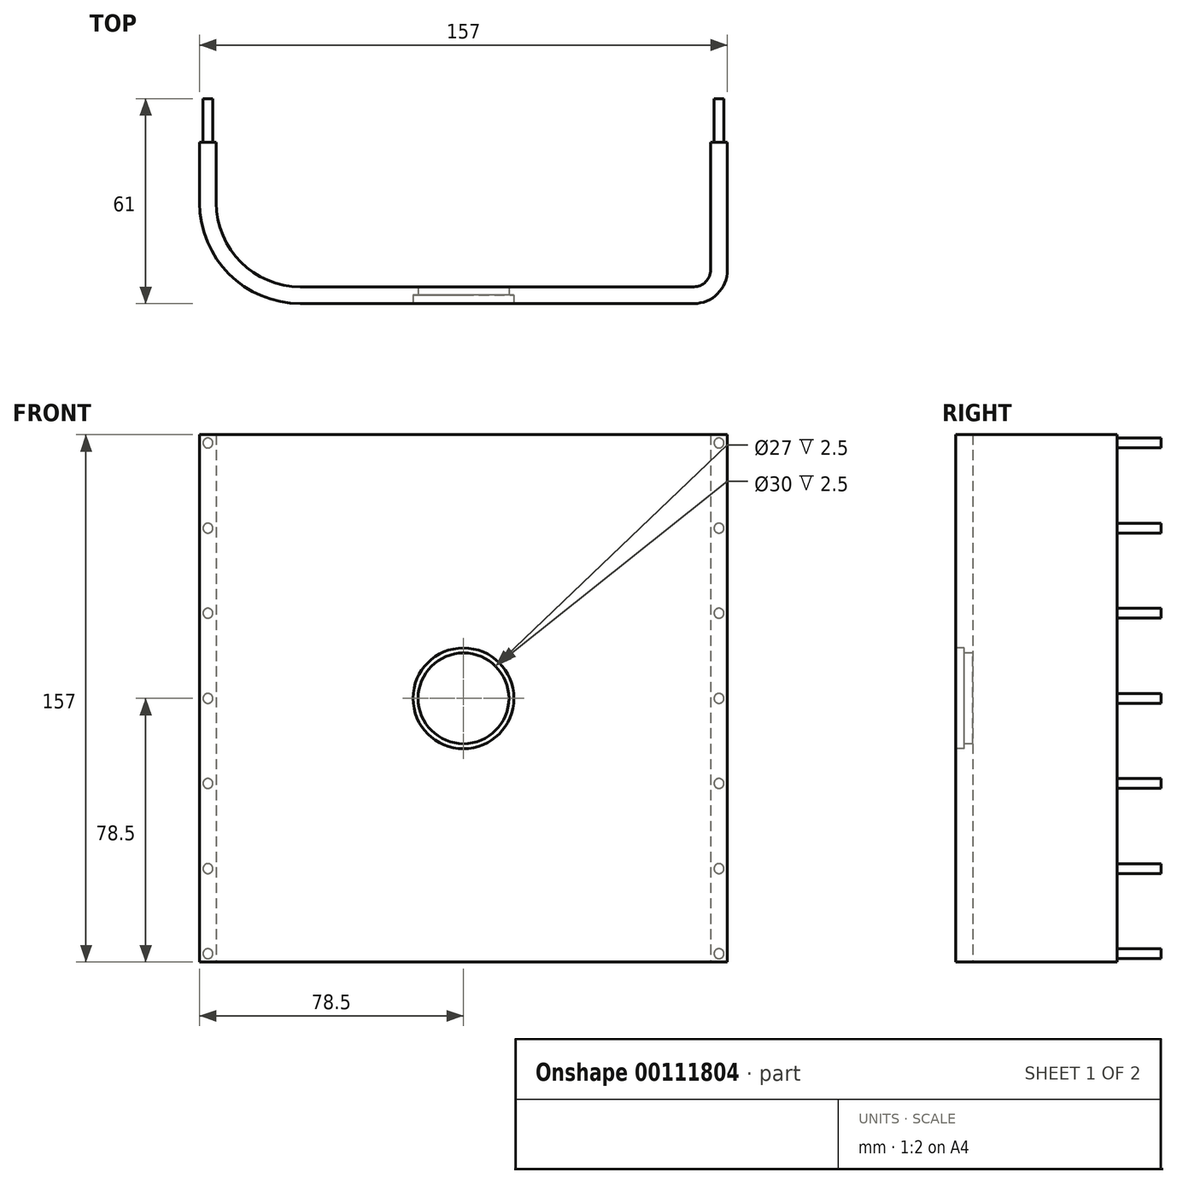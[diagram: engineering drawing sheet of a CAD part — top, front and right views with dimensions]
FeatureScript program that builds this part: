
annotation { "Feature Type Name" : "Feature", "Feature Type Description" : "" }
export const myFeature = defineFeature(function(context is Context, id is Id, definition is map)
    precondition{}
    {
        {
            var Q0;
            Q0=qCreatedBy(makeId("Top.planeOp"),FACE);
            var sketch = newSketch(context, id + "F0", { "sketchPlane" : qUnion([Q0])});
            skLineSegment(sketch, "E0.bottom", {"start": v(68.5, -24) * mm, "end": v(-48.5, -24) * mm});
            skLineSegment(sketch, "E0.top", {"start": v(78.5, 24) * mm, "end": v(-78.5, 24) * mm});
            skLineSegment(sketch, "E0.left", {"start": v(78.5, -14) * mm, "end": v(78.5, 24) * mm});
            skLineSegment(sketch, "E0.right", {"start": v(-78.5, 6) * mm, "end": v(-78.5, 24) * mm});
            skPoint(sketch, "E0.middle", {"position": v(0, 0) * mm});
            skPoint(sketch, "E1.visualSharp", {"position": v(78.5, -24) * mm});
            skArc(sketch, "E1.filletArc", {"start": v(68.5, -24) * mm, "mid": v(75.57, -21.07) * mm, "end": v(78.5, -14) * mm});
            skPoint(sketch, "E2.visualSharp", {"position": v(-78.5, -24) * mm});
            skArc(sketch, "E2.filletArc", {"start": v(-78.5, 6) * mm, "mid": v(-69.71, -15.21) * mm, "end": v(-48.5, -24) * mm});
            skLineSegment(sketch, "E3.bottom", {"start": v(68.5, -19) * mm, "end": v(-48.5, -19) * mm});
            skLineSegment(sketch, "E3.left", {"start": v(73.5, -14) * mm, "end": v(73.5, 24) * mm});
            skLineSegment(sketch, "E3.right", {"start": v(-73.5, 6) * mm, "end": v(-73.5, 24) * mm});
            skPoint(sketch, "E4.visualSharp", {"position": v(-73.5, -19) * mm});
            skArc(sketch, "E4.filletArc", {"start": v(-73.5, 6) * mm, "mid": v(-66.18, -11.68) * mm, "end": v(-48.5, -19) * mm});
            skPoint(sketch, "E5.visualSharp", {"position": v(73.5, -19) * mm});
            skArc(sketch, "E5.filletArc", {"start": v(68.5, -19) * mm, "mid": v(72.04, -17.54) * mm, "end": v(73.5, -14) * mm});
            skSolve(sketch);
        }
        {
            var Q0;
            Q0=makeQuery(id+"F0.imprint","IMPRINT",FACE,{"disambiguationData":[TD([[makeQuery(id+"F0.imprint","IMPRINT",EDGE,{"derivedFrom":sQuery(id+"F0.wireOp",EDGE,"E0.bottom")}),-1.0]])]});
            extrude(context, id + "F1", {"entities" : qUnion([Q0]), "depth" : 157 * mm});
        }
        {
            var Q0;
            Q0=makeQuery(id+"F1.opExtrude","SWEPT_FACE",FACE,{"disambiguationData":[OSD([sQuery(id+"F0.wireOp",EDGE,"E0.bottom")])]});
            var sketch = newSketch(context, id + "F2", { "sketchPlane" : qUnion([Q0])});
            skCircle(sketch, "E6", {"center": v(0, 78.5) * mm, "radius": 13.5 * mm});
            skSolve(sketch);
        }
        {
            var Q0;
            Q0=makeQuery(id+"F2.imprint","IMPRINT",FACE,{"disambiguationData":[TD([[makeQuery(id+"F2.imprint","IMPRINT",EDGE,{"derivedFrom":sQuery(id+"F2.wireOp",EDGE,"E6")}),1.0]])]});
            extrude(context, id + "F3", {"entities" : qUnion([Q0]), "operationType" : NewBodyOperationType.REMOVE, "oppositeDirection" : true, "depth" : 25 * mm});
        }
        {
            var Q0;
            Q0=makeQuery(id+"F1.opExtrude","SWEPT_FACE",FACE,{"disambiguationData":[OSD([sQuery(id+"F0.wireOp",EDGE,"E0.bottom")])]});
            var sketch = newSketch(context, id + "F4", { "sketchPlane" : qUnion([Q0])});
            skCircle(sketch, "E7", {"center": v(0, 78.5) * mm, "radius": 15 * mm});
            skSolve(sketch);
        }
        {
            var Q0;
            Q0 = qSketchRegion(id + "F4", true);
            extrude(context, id + "F5", {"entities" : qUnion([Q0]), "operationType" : NewBodyOperationType.REMOVE, "oppositeDirection" : true, "depth" : 2.5 * mm});
        }
        {
            var Q0;
            {var subQ0=sQuery(id+"F0.wireOp",EDGE,"E0.top");Q0=makeQuery(id+"F1.opExtrude","SWEPT_FACE",FACE,{"disambiguationData":[OSD([subQ0]),TDD([makeQuery(id+"F0.imprint","IMPRINT",EDGE,{"disambiguationData":[TD([[makeQuery(id+"F0.imprint","INTERSECT",VERTEX,{"derivedFrom":[subQ0,sQuery(id+"F0.wireOp",EDGE,"E0.right")]}),1.0]])],"derivedFrom":subQ0})])]});}
            var sketch = newSketch(context, id + "F6", { "sketchPlane" : qUnion([Q0])});
            skCircle(sketch, "E8", {"center": v(-76, 154.5) * mm, "radius": 1.48 * mm});
            skCircle(sketch, "E9.0.1.0", {"center": v(-76, 129.17) * mm, "radius": 1.48 * mm});
            skCircle(sketch, "E9.0.2.0", {"center": v(-76, 103.83) * mm, "radius": 1.48 * mm});
            skCircle(sketch, "E9.0.3.0", {"center": v(-76, 78.5) * mm, "radius": 1.48 * mm});
            skCircle(sketch, "E9.0.4.0", {"center": v(-76, 53.17) * mm, "radius": 1.48 * mm});
            skCircle(sketch, "E9.0.5.0", {"center": v(-76, 27.83) * mm, "radius": 1.48 * mm});
            skCircle(sketch, "E9.0.6.0", {"center": v(-76, 2.5) * mm, "radius": 1.48 * mm});
            skLineSegment(sketch, "E9.direction1", {"start": v(-76, 154.5) * mm, "end": v(-51, 154.5) * mm, "construction": true});
            skLineSegment(sketch, "E9.direction2", {"start": v(-76, 154.5) * mm, "end": v(-76, 129.17) * mm, "construction": true});
            skSolve(sketch);
        }
        {
            var Q0;
            Q0 = qSketchRegion(id + "F6", true);
            extrude(context, id + "F7", {"entities" : qUnion([Q0]), "operationType" : NewBodyOperationType.ADD, "depth" : 13 * mm});
        }
        {
            var Q0;
            {var subQ0=sQuery(id+"F0.wireOp",EDGE,"E0.top");Q0=makeQuery(id+"F1.opExtrude","SWEPT_FACE",FACE,{"disambiguationData":[OSD([subQ0]),TDD([makeQuery(id+"F0.imprint","IMPRINT",EDGE,{"disambiguationData":[TD([[makeQuery(id+"F0.imprint","INTERSECT",VERTEX,{"derivedFrom":[subQ0,sQuery(id+"F0.wireOp",EDGE,"E0.right")]}),1.0]])],"derivedFrom":subQ0})])]});}
            var sketch = newSketch(context, id + "F8", { "sketchPlane" : qUnion([Q0])});
            skCircle(sketch, "E10", {"center": v(76, 154.5) * mm, "radius": 1.48 * mm});
            skCircle(sketch, "E11.0.1.0", {"center": v(76, 129.17) * mm, "radius": 1.48 * mm});
            skCircle(sketch, "E11.0.2.0", {"center": v(76, 103.83) * mm, "radius": 1.48 * mm});
            skCircle(sketch, "E11.0.3.0", {"center": v(76, 78.5) * mm, "radius": 1.48 * mm});
            skCircle(sketch, "E11.0.4.0", {"center": v(76, 53.17) * mm, "radius": 1.48 * mm});
            skCircle(sketch, "E11.0.5.0", {"center": v(76, 27.83) * mm, "radius": 1.48 * mm});
            skCircle(sketch, "E11.0.6.0", {"center": v(76, 2.5) * mm, "radius": 1.48 * mm});
            skLineSegment(sketch, "E11.direction1", {"start": v(76, 154.5) * mm, "end": v(101, 154.5) * mm, "construction": true});
            skLineSegment(sketch, "E11.direction2", {"start": v(76, 154.5) * mm, "end": v(76, 129.17) * mm, "construction": true});
            skSolve(sketch);
        }
        {
            var Q0;
            Q0=makeQuery(id+"F8.imprint","IMPRINT",FACE,{"disambiguationData":[TD([[makeQuery(id+"F8.imprint","IMPRINT",EDGE,{"derivedFrom":sQuery(id+"F8.wireOp",EDGE,"E11.0.2.0")}),1.0]])]});
            var Q1;
            Q1=makeQuery(id+"F8.imprint","IMPRINT",FACE,{"disambiguationData":[TD([[makeQuery(id+"F8.imprint","IMPRINT",EDGE,{"derivedFrom":sQuery(id+"F8.wireOp",EDGE,"E11.0.1.0")}),1.0]])]});
            var Q2;
            Q2=makeQuery(id+"F8.imprint","IMPRINT",FACE,{"disambiguationData":[TD([[makeQuery(id+"F8.imprint","IMPRINT",EDGE,{"derivedFrom":sQuery(id+"F8.wireOp",EDGE,"E10")}),1.0]])]});
            var Q3;
            Q3=makeQuery(id+"F8.imprint","IMPRINT",FACE,{"disambiguationData":[TD([[makeQuery(id+"F8.imprint","IMPRINT",EDGE,{"derivedFrom":sQuery(id+"F8.wireOp",EDGE,"E11.0.3.0")}),1.0]])]});
            var Q4;
            Q4=makeQuery(id+"F8.imprint","IMPRINT",FACE,{"disambiguationData":[TD([[makeQuery(id+"F8.imprint","IMPRINT",EDGE,{"derivedFrom":sQuery(id+"F8.wireOp",EDGE,"E11.0.4.0")}),1.0]])]});
            var Q5;
            Q5=makeQuery(id+"F8.imprint","IMPRINT",FACE,{"disambiguationData":[TD([[makeQuery(id+"F8.imprint","IMPRINT",EDGE,{"derivedFrom":sQuery(id+"F8.wireOp",EDGE,"E11.0.6.0")}),1.0]])]});
            var Q6;
            Q6=makeQuery(id+"F8.imprint","IMPRINT",FACE,{"disambiguationData":[TD([[makeQuery(id+"F8.imprint","IMPRINT",EDGE,{"derivedFrom":sQuery(id+"F8.wireOp",EDGE,"E11.0.5.0")}),1.0]])]});
            extrude(context, id + "F9", {"entities" : qUnion([Q0, Q1, Q2, Q3, Q4, Q5, Q6]), "operationType" : NewBodyOperationType.ADD, "depth" : 13 * mm});
        }
    });
